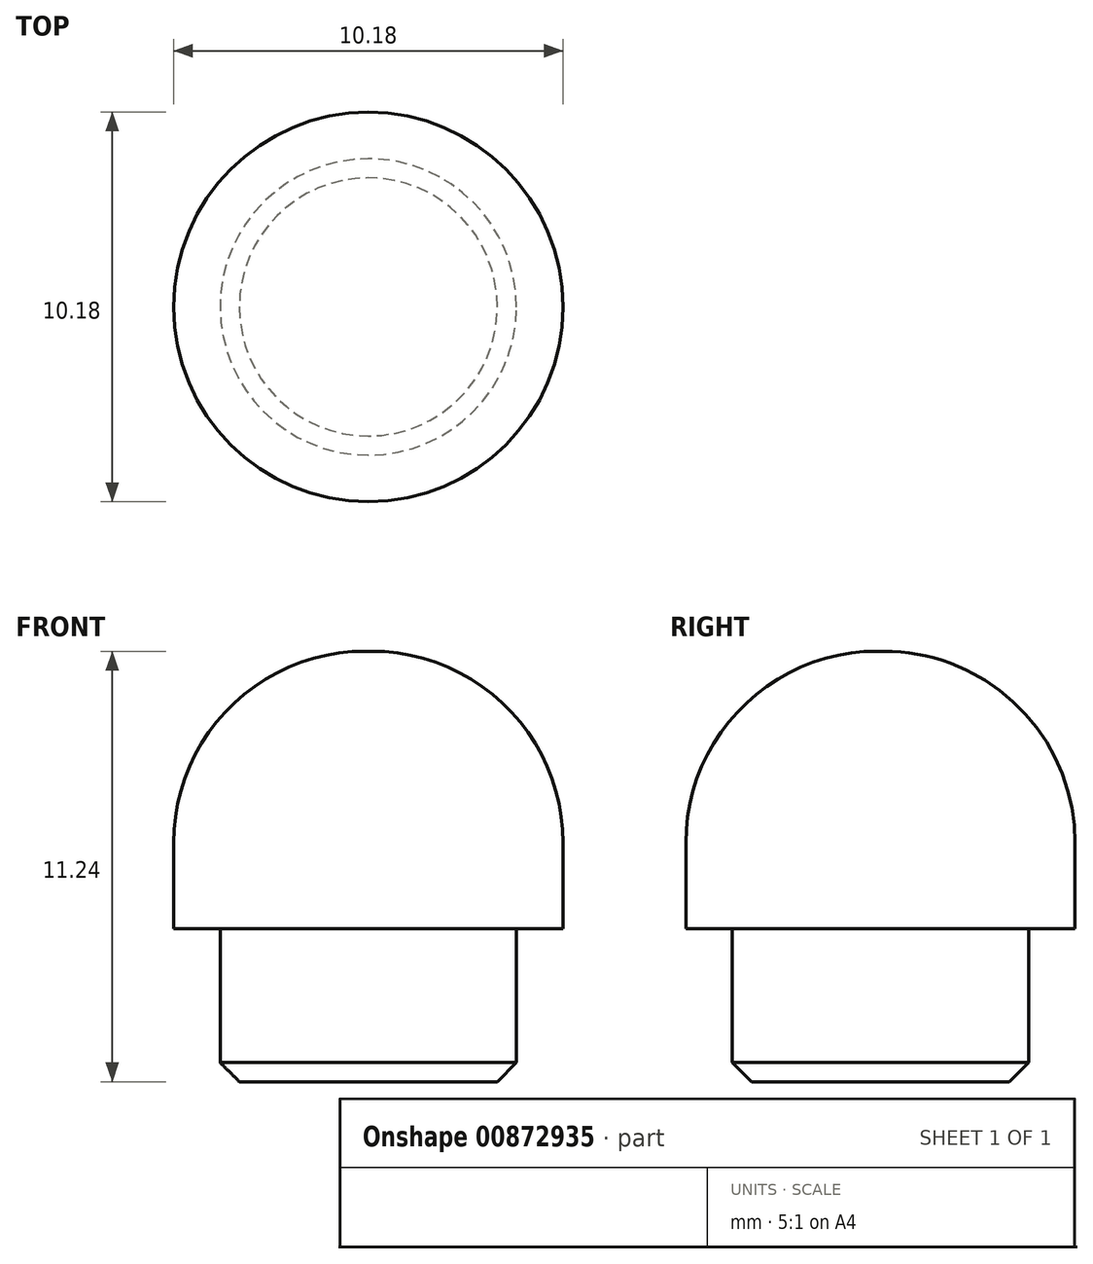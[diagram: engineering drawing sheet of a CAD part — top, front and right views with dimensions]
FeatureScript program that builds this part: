
annotation { "Feature Type Name" : "Feature", "Feature Type Description" : "" }
export const myFeature = defineFeature(function(context is Context, id is Id, definition is map)
    precondition{}
    {
        {
            var Q0;
            Q0=qCreatedBy(makeId("Top.planeOp"),FACE);
            var sketch = newSketch(context, id + "F0", { "sketchPlane" : qUnion([Q0])});
            skCircle(sketch, "E0", {"center": v(0, 0) * mm, "radius": 5.09 * mm});
            skSolve(sketch);
        }
        {
            var Q0;
            Q0 = qSketchRegion(id + "F0", true);
            extrude(context, id + "F1", {"entities" : qUnion([Q0]), "depth" : 7.24 * mm, "offsetDistance" : 25 * mm});
        }
        {
            var Q0;
            Q0=makeQuery(id+"F1.opExtrude","CAP_EDGE",EDGE,{"disambiguationData":[OSD([sQuery(id+"F0.wireOp",EDGE,"E0")])],"isStart":false});
            fillet(context, id + "F2", {"entities" : qUnion([Q0]), "radius" : 5 * mm, "tangentPropagation" : true, "allowEdgeOverflow" : false});
        }
        {
            var Q0;
            Q0=makeQuery(id+"F1.opExtrude","CAP_FACE",FACE,{"disambiguationData":[OSD([sQuery(id+"F0.wireOp",EDGE,"E0")])],"isStart":true});
            var sketch = newSketch(context, id + "F3", { "sketchPlane" : qUnion([Q0])});
            skCircle(sketch, "E1", {"center": v(0, 0) * mm, "radius": 3.87 * mm});
            skSolve(sketch);
        }
        {
            var Q0;
            Q0 = qSketchRegion(id + "F3", true);
            extrude(context, id + "F4", {"entities" : qUnion([Q0]), "operationType" : NewBodyOperationType.ADD, "depth" : 4 * mm, "offsetDistance" : 25 * mm});
        }
        {
            var Q0;
            Q0=makeQuery(id+"F4.opExtrude","CAP_EDGE",EDGE,{"disambiguationData":[OSD([sQuery(id+"F3.wireOp",EDGE,"E1")])],"isStart":false});
            chamfer(context, id + "F5", {"entities" : qUnion([Q0]), "width" : .5 * mm, "tangentPropagation" : true});
        }
    });
